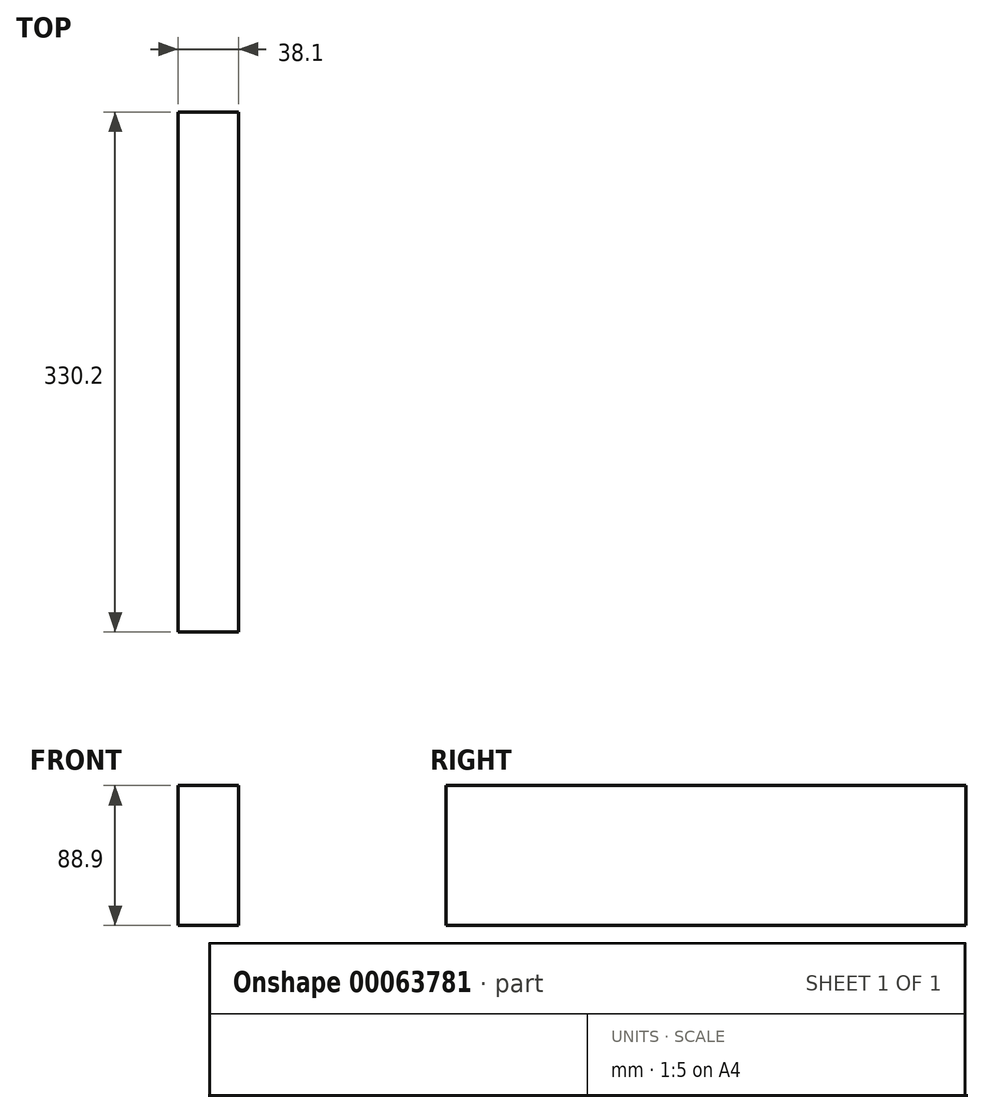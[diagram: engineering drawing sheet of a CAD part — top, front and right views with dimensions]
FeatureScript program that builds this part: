
annotation { "Feature Type Name" : "Feature", "Feature Type Description" : "" }
export const myFeature = defineFeature(function(context is Context, id is Id, definition is map)
    precondition{}
    {
        {
            var Q0;
            Q0=qCreatedBy(makeId("Front.planeOp"),FACE);
            var sketch = newSketch(context, id + "F0", { "sketchPlane" : qUnion([Q0])});
            skLineSegment(sketch, "E0.bottom", {"start": v(-18, 55.77) * mm, "end": v(20.1, 55.77) * mm});
            skLineSegment(sketch, "E0.top", {"start": v(-18, -33.13) * mm, "end": v(20.1, -33.13) * mm});
            skLineSegment(sketch, "E0.left", {"start": v(-18, 55.77) * mm, "end": v(-18, -33.13) * mm});
            skLineSegment(sketch, "E0.right", {"start": v(20.1, 55.77) * mm, "end": v(20.1, -33.13) * mm});
            skSolve(sketch);
        }
        {
            var Q0;
            Q0=qSketchRegion(id+"F0",true);
            extrude(context, id + "F1", {"entities" : qUnion([Q0]), "endBound" : BoundingType.SYMMETRIC, "depth" : 330.2 * mm});
        }
    });
